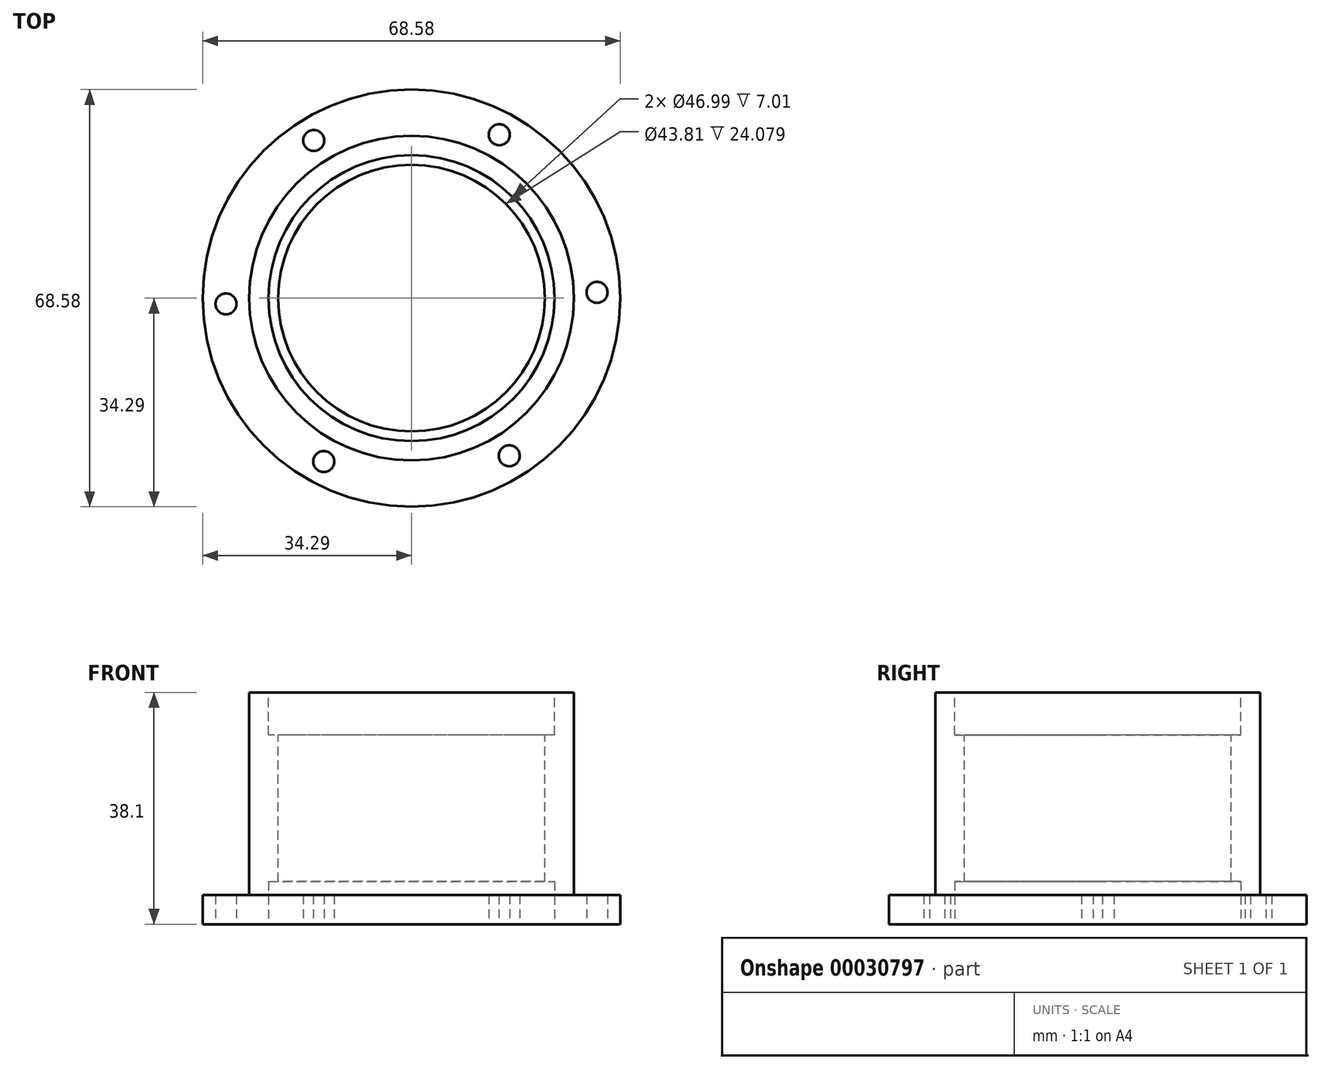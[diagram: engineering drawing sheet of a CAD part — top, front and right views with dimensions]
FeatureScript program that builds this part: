
annotation { "Feature Type Name" : "Feature", "Feature Type Description" : "" }
export const myFeature = defineFeature(function(context is Context, id is Id, definition is map)
    precondition{}
    {
        {
            var Q0;
            Q0=qCreatedBy(makeId("Top.planeOp"),FACE);
            var sketch = newSketch(context, id + "F0", { "sketchPlane" : qUnion([Q0])});
            skCircle(sketch, "E0", {"center": v(0, 0) * mm, "radius": 34.3 * mm});
            skSolve(sketch);
        }
        {
            var Q0;
            Q0 = qSketchRegion(id + "F0", true);
            extrude(context, id + "F1", {"entities" : qUnion([Q0]), "depth" : 4.78 * mm});
        }
        {
            var Q0;
            Q0=makeQuery(id+"F1.opExtrude","CAP_FACE",FACE,{"disambiguationData":[OSD([sQuery(id+"F0.wireOp",EDGE,"E0")])],"isStart":false});
            var sketch = newSketch(context, id + "F2", { "sketchPlane" : qUnion([Q0])});
            skCircle(sketch, "E1", {"center": v(0, 0) * mm, "radius": 26.67 * mm});
            skSolve(sketch);
        }
        {
            var Q0;
            Q0 = qSketchRegion(id + "F2", true);
            extrude(context, id + "F3", {"entities" : qUnion([Q0]), "operationType" : NewBodyOperationType.ADD, "depth" : 33.32 * mm});
        }
        {
            var Q0;
            Q0=makeQuery(id+"F3.opExtrude","CAP_FACE",FACE,{"disambiguationData":[OSD([sQuery(id+"F2.wireOp",EDGE,"E1")])],"isStart":false});
            var sketch = newSketch(context, id + "F4", { "sketchPlane" : qUnion([Q0])});
            skCircle(sketch, "E2", {"center": v(0, 0) * mm, "radius": 21.9 * mm});
            skSolve(sketch);
        }
        {
            var Q0;
            Q0=makeQuery(id+"F4.imprint","IMPRINT",FACE,{"disambiguationData":[TD([[makeQuery(id+"F4.imprint","IMPRINT",EDGE,{"derivedFrom":sQuery(id+"F4.wireOp",EDGE,"E2")}),1.0]])]});
            extrude(context, id + "F5", {"entities" : qUnion([Q0]), "operationType" : NewBodyOperationType.REMOVE, "endBound" : BoundingType.THROUGH_ALL, "oppositeDirection" : true, "depth" : 25.4 * mm});
        }
        {
            var Q0;
            Q0=makeQuery(id+"F3.opExtrude","CAP_FACE",FACE,{"disambiguationData":[OSD([sQuery(id+"F2.wireOp",EDGE,"E1")])],"isStart":false});
            var sketch = newSketch(context, id + "F6", { "sketchPlane" : qUnion([Q0])});
            skCircle(sketch, "E3", {"center": v(0, 0) * mm, "radius": 23.5 * mm});
            skSolve(sketch);
        }
        {
            var Q0;
            Q0=makeQuery(id+"F6.imprint","IMPRINT",FACE,{"disambiguationData":[TD([[makeQuery(id+"F6.imprint","IMPRINT",EDGE,{"derivedFrom":sQuery(id+"F6.wireOp",EDGE,"E3")}),1.0]])]});
            extrude(context, id + "F7", {"entities" : qUnion([Q0]), "operationType" : NewBodyOperationType.REMOVE, "oppositeDirection" : true, "depth" : 7 * mm});
        }
        {
            var Q0;
            Q0=makeQuery(id+"F1.opExtrude","CAP_FACE",FACE,{"disambiguationData":[OSD([sQuery(id+"F0.wireOp",EDGE,"E0")])],"isStart":true});
            var sketch = newSketch(context, id + "F8", { "sketchPlane" : qUnion([Q0])});
            skCircle(sketch, "E4", {"center": v(0, 0) * mm, "radius": 23.5 * mm});
            skSolve(sketch);
        }
        {
            var Q0;
            Q0=makeQuery(id+"F8.imprint","IMPRINT",FACE,{"disambiguationData":[TD([[makeQuery(id+"F8.imprint","IMPRINT",EDGE,{"derivedFrom":sQuery(id+"F8.wireOp",EDGE,"E4")}),1.0]])]});
            extrude(context, id + "F9", {"entities" : qUnion([Q0]), "operationType" : NewBodyOperationType.REMOVE, "oppositeDirection" : true, "depth" : 7 * mm});
        }
        {
            var Q0;
            Q0=makeQuery(id+"F1.opExtrude","CAP_FACE",FACE,{"disambiguationData":[OSD([sQuery(id+"F0.wireOp",EDGE,"E0")])],"isStart":true});
            var sketch = newSketch(context, id + "F10", { "sketchPlane" : qUnion([Q0])});
            skCircle(sketch, "E5.cCircle", {"center": v(0, 0) * mm, "radius": 30.48 * mm, "construction": true});
            skLineSegment(sketch, "E5.0", {"start": v(30.47, -0.95) * mm, "end": v(14.41, -26.86) * mm});
            skLineSegment(sketch, "E5.1", {"start": v(14.41, -26.86) * mm, "end": v(-16.05, -25.91) * mm});
            skLineSegment(sketch, "E5.2", {"start": v(-16.05, -25.91) * mm, "end": v(-30.47, 0.95) * mm});
            skLineSegment(sketch, "E5.3", {"start": v(-30.47, 0.95) * mm, "end": v(-14.41, 26.86) * mm});
            skLineSegment(sketch, "E5.4", {"start": v(-14.41, 26.86) * mm, "end": v(16.05, 25.91) * mm});
            skLineSegment(sketch, "E5.5", {"start": v(16.05, 25.91) * mm, "end": v(30.47, -0.95) * mm});
            skSolve(sketch);
        }
        {
            var Q0;
            Q0=sQuery(id+"F10.wireOp",VERTEX,"E5.2.start");
            var Q1;
            Q1=sQuery(id+"F10.wireOp",VERTEX,"E5.3.start");
            var Q2;
            Q2=sQuery(id+"F10.wireOp",VERTEX,"E5.4.start");
            var Q3;
            Q3=sQuery(id+"F10.wireOp",VERTEX,"E5.4.end");
            var Q4;
            Q4=sQuery(id+"F10.wireOp",VERTEX,"E5.0.start");
            var Q5;
            Q5=sQuery(id+"F10.wireOp",VERTEX,"E5.1.start");
            var Q6;
            Q6=makeQuery(id+"F1.opExtrude","SWEPT_BODY",BODY,{"disambiguationData":[OSD([sQuery(id+"F0.wireOp",EDGE,"E0")])]});
            hole(context, id + "F11", {"style" : HoleStyle.SIMPLE, "holeDiameter" : 3.45 * mm, "endStyle" : HoleEndStyle.THROUGH, "locations" : qUnion([Q0, Q1, Q2, Q3, Q4, Q5]), "scope" : qUnion([Q6])});
        }
    });
